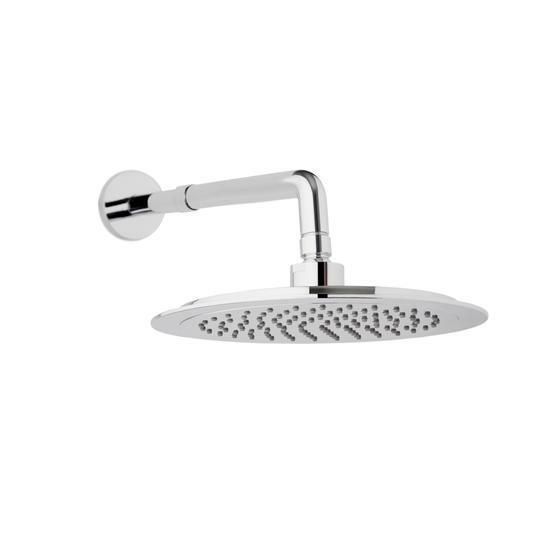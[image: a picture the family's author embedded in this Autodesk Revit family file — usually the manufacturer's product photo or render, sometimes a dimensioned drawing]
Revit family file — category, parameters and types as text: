
# Revit family: BL-8630-11 REGADERA ISEO REDONDA 22 CM
name_source: partatom
category: Plumbing Fixtures
revit_build: Autodesk Revit 2018 (Build: 20170223_1515(x64)
units: mm (PartAtom-declared; Revit-internal decimal feet)

## family parameters
Cut with Voids When Loaded = No
Host = Face
OmniClass Number = 23.31.11.00
Part Type = Normal
Room Calculation Point = No
Round Connector Dimension = Use Diameter
Shared = No

## types (1)
- BL-8630-11
    Alto = 175 mm
    CW Connection = Yes
    Default Elevation = 0 mm  [stored 0 ft]
    Description = Regadera
    Diametro = 232 mm
    HW Connection = Yes
    Link Ficha Tecnica = http://infotecnica.gricol.com
    Manufacturer = Gricol
    Model = BL-8630-11
    Plastico ABS Cromado = Plastico ABS Cromado
    Product Name = REGADERA ISEO REDONDA 22 CM
    Profundidad = 350 mm  [stored 1.14829 ft]
    Type Image = <None>
    URL = https://www.gricol.com
    Vent Connection = No
    Waste Connection = No

note: [stored X ft] marks values corroborated as IEEE doubles in the binary element streams (Revit-internal decimal feet)

## geometry (parser evidence)
native form markers: Blend x2, Sweep x16
no freeform markers — native parametric forms only
